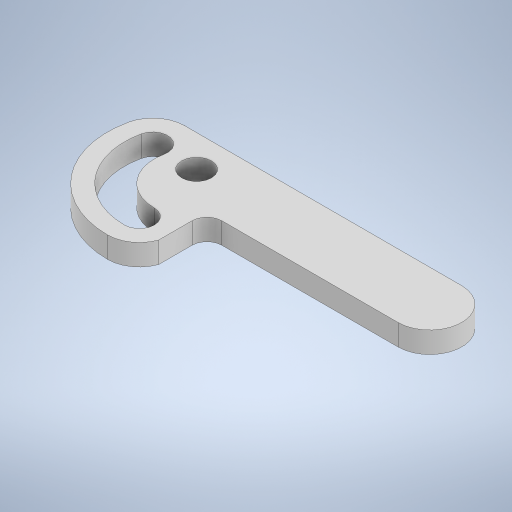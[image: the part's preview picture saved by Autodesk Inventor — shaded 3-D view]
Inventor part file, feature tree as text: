
AUTODESK INVENTOR PART (.ipt)
format: ipt  version: 2023.2 (Build 272271000, 271)  size: 258,048 bytes
history: native  units: mm
features: extrude x1, sketch x1
ambient origin geometry x8: Origin, YZ Plane, XZ Plane, XY Plane, X Axis, Y Axis, Z Axis, Center Point
bodies: Solid1 (feature_tree)
feature tree (2):
  extrude  "Extrusion1"  Depth=130.51mm
  sketch  "Sketch1"  dims[d0=30.0mm d1=130.51mm d2=90.0mm d3=15.0mm d4=14.0mm d5=20.63mm d6=14.0mm d9=20.0mm d11=14.0mm d12=15.0mm d13=42.0mm d14=7.0mm d15=10.0mm d16=0.0mm]
